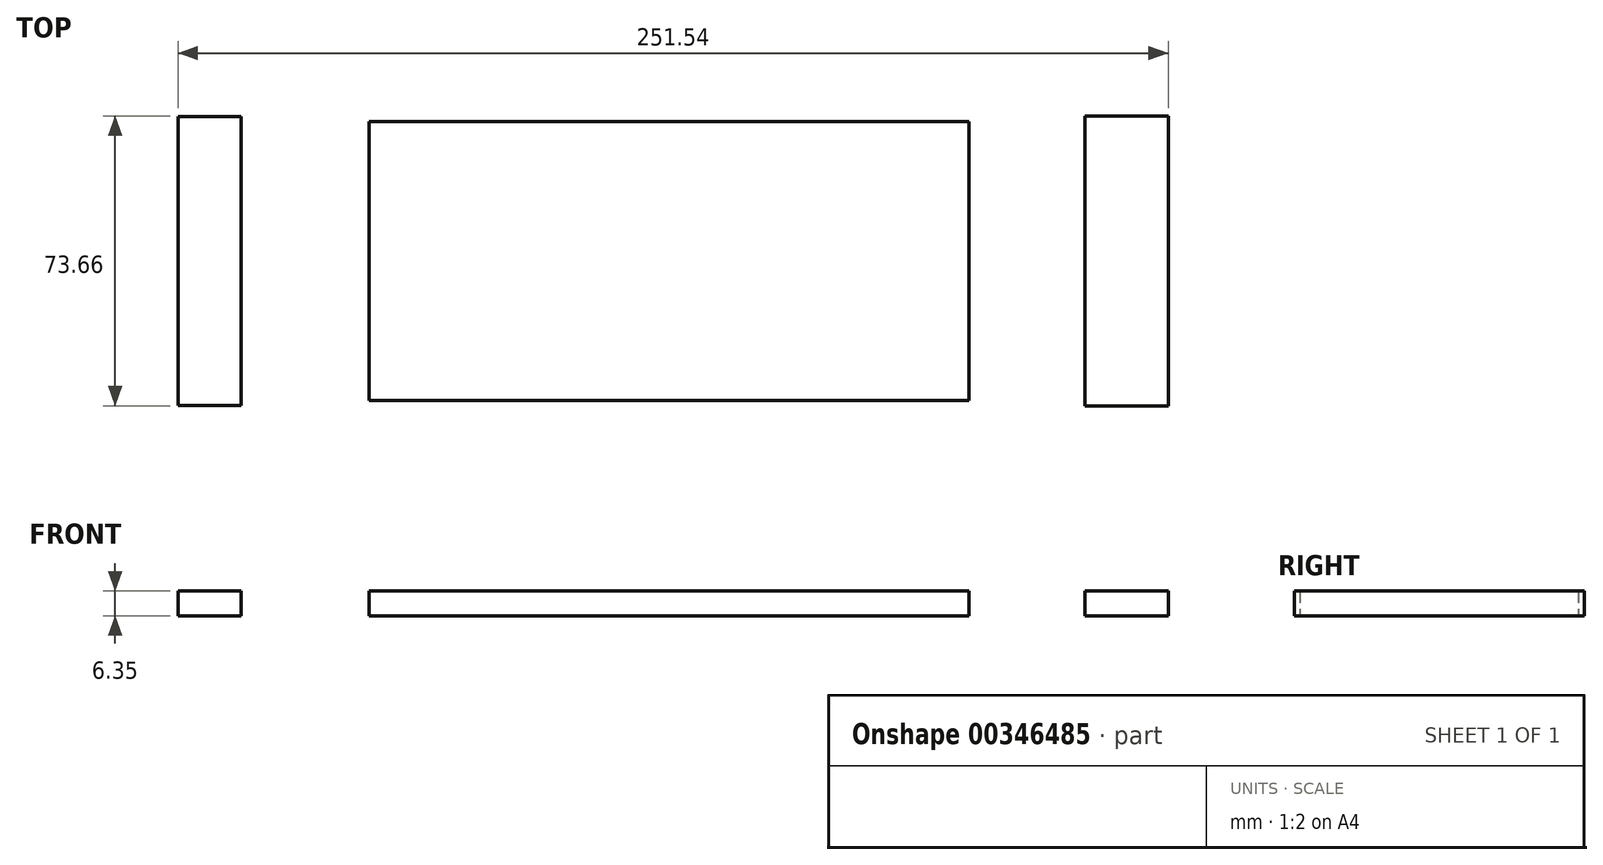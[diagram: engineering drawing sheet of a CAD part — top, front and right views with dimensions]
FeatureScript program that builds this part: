
annotation { "Feature Type Name" : "Feature", "Feature Type Description" : "" }
export const myFeature = defineFeature(function(context is Context, id is Id, definition is map)
    precondition{}
    {
        {
            var Q0;
            Q0=qCreatedBy(makeId("Top.planeOp"),FACE);
            var sketch = newSketch(context, id + "F0", { "sketchPlane" : qUnion([Q0])});
            skLineSegment(sketch, "E0.bottom", {"start": v(-76.2, -35.42) * mm, "end": v(76.2, -35.42) * mm});
            skLineSegment(sketch, "E0.top", {"start": v(-76.2, 35.42) * mm, "end": v(76.2, 35.42) * mm});
            skLineSegment(sketch, "E0.left", {"start": v(-76.2, -35.42) * mm, "end": v(-76.2, 35.42) * mm});
            skLineSegment(sketch, "E0.right", {"start": v(76.2, -35.42) * mm, "end": v(76.2, 35.42) * mm});
            skPoint(sketch, "E0.middle", {"position": v(0, 0) * mm});
            skLineSegment(sketch, "E1.bottom", {"start": v(-124.73, -36.7) * mm, "end": v(-108.66, -36.7) * mm});
            skLineSegment(sketch, "E1.top", {"start": v(-124.73, 36.7) * mm, "end": v(-108.66, 36.7) * mm});
            skLineSegment(sketch, "E1.left", {"start": v(-124.73, -36.7) * mm, "end": v(-124.73, 36.7) * mm});
            skLineSegment(sketch, "E1.right", {"start": v(-108.66, -36.7) * mm, "end": v(-108.66, 36.7) * mm});
            skPoint(sketch, "E1.middle", {"position": v(-116.7, 0) * mm});
            skLineSegment(sketch, "E2.bottom", {"start": v(126.8, -36.83) * mm, "end": v(105.65, -36.83) * mm});
            skLineSegment(sketch, "E2.top", {"start": v(126.8, 36.83) * mm, "end": v(105.65, 36.83) * mm});
            skLineSegment(sketch, "E2.left", {"start": v(126.8, -36.83) * mm, "end": v(126.8, 36.83) * mm});
            skLineSegment(sketch, "E2.right", {"start": v(105.65, -36.83) * mm, "end": v(105.65, 36.83) * mm});
            skPoint(sketch, "E2.middle", {"position": v(116.23, 0) * mm});
            skLineSegment(sketch, "E3", {"start": v(-115.9, 0.49) * mm, "end": v(0, 0) * mm});
            skLineSegment(sketch, "E4", {"start": v(0, 0) * mm, "end": v(116.23, 0) * mm});
            skSolve(sketch);
        }
        {
            var Q0;
            Q0 = qSketchRegion(id + "F0", true);
            extrude(context, id + "F1", {"entities" : qUnion([Q0]), "depth" : 6.35 * mm});
        }
    });
